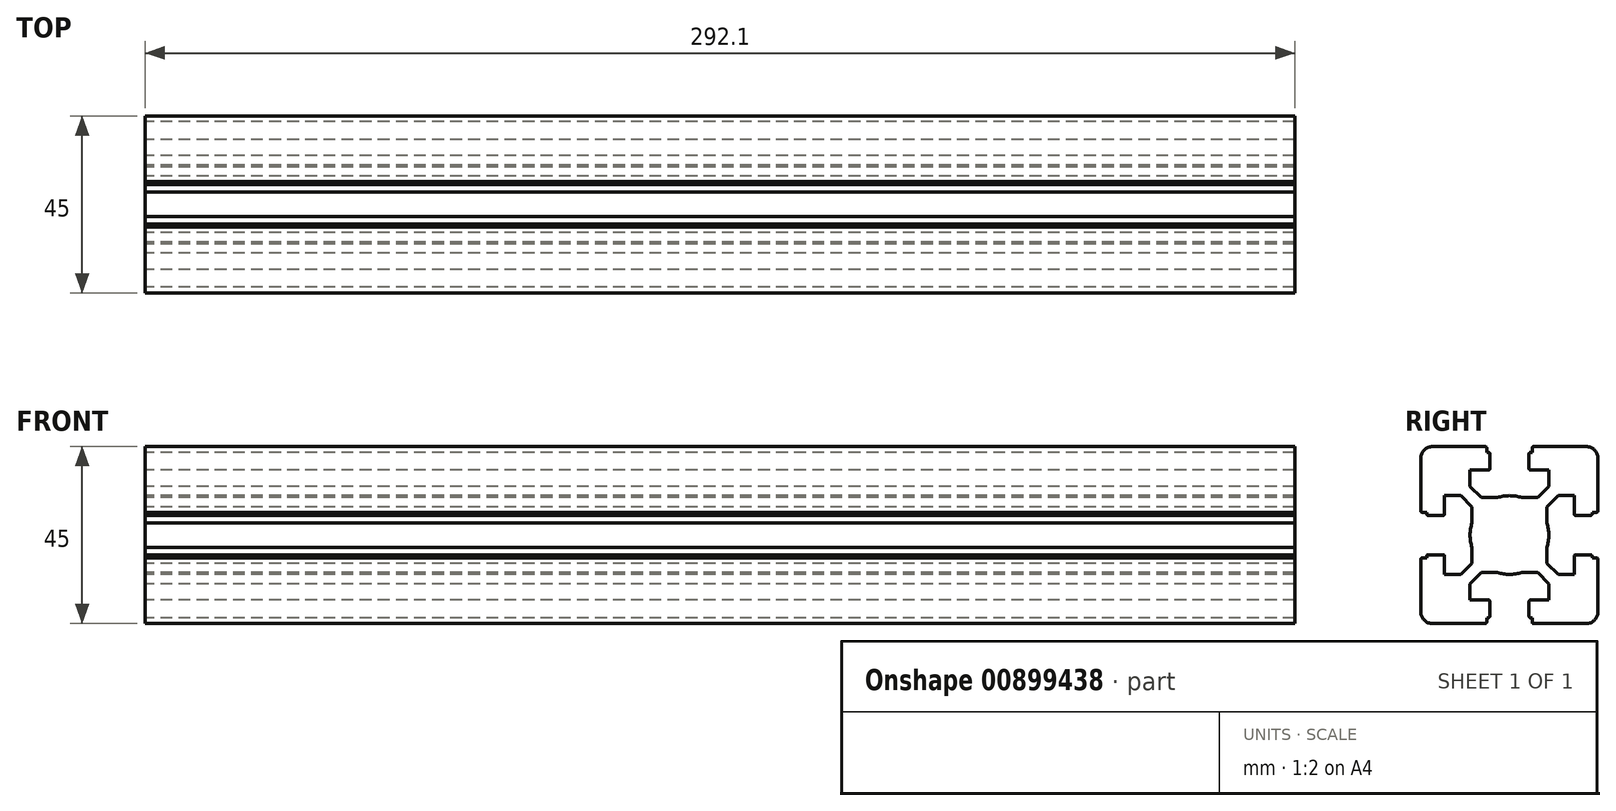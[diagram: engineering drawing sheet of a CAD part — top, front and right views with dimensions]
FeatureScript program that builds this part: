
annotation { "Feature Type Name" : "Feature", "Feature Type Description" : "" }
export const myFeature = defineFeature(function(context is Context, id is Id, definition is map)
    precondition{}
    {
        {
            var Q0;
            Q0=qCreatedBy(makeId("Right.planeOp"),FACE);
            var sketch = newSketch(context, id + "F0", { "sketchPlane" : qUnion([Q0])});
            skLineSegment(sketch, "E0", {"start": v(-20.09, -10.29) * mm, "end": v(-21.29, -10.29) * mm});
            skArc(sketch, "E1", {"start": v(-21.29, -10.29) * mm, "mid": v(-21.5, -10.38) * mm, "end": v(-21.59, -10.59) * mm});
            skLineSegment(sketch, "E2", {"start": v(-21.59, -10.59) * mm, "end": v(-21.59, -23.99) * mm});
            skArc(sketch, "E3", {"start": v(-21.59, -23.99) * mm, "mid": v(-20.7, -26.11) * mm, "end": v(-18.59, -26.99) * mm});
            skLineSegment(sketch, "E4", {"start": v(-18.59, -26.99) * mm, "end": v(-5.19, -26.99) * mm});
            skArc(sketch, "E5", {"start": v(-5.19, -26.99) * mm, "mid": v(-4.98, -26.9) * mm, "end": v(-4.89, -26.69) * mm});
            skLineSegment(sketch, "E6", {"start": v(-4.89, -26.69) * mm, "end": v(-4.89, -25.49) * mm});
            skLineSegment(sketch, "E7", {"start": v(-4.89, -25.49) * mm, "end": v(-4.39, -25.49) * mm});
            skArc(sketch, "E8", {"start": v(-4.39, -25.49) * mm, "mid": v(-4.18, -25.4) * mm, "end": v(-4.09, -25.19) * mm});
            skLineSegment(sketch, "E9", {"start": v(-4.09, -25.19) * mm, "end": v(-4.09, -21.29) * mm});
            skArc(sketch, "E10", {"start": v(-4.09, -21.29) * mm, "mid": v(-4.18, -21.08) * mm, "end": v(-4.39, -20.99) * mm});
            skLineSegment(sketch, "E11", {"start": v(-4.39, -20.99) * mm, "end": v(-9.14, -20.99) * mm});
            skLineSegment(sketch, "E12", {"start": v(-9.14, -20.99) * mm, "end": v(-9.14, -16.88) * mm});
            skLineSegment(sketch, "E13", {"start": v(-9.14, -16.88) * mm, "end": v(-6.25, -13.99) * mm});
            skLineSegment(sketch, "E14", {"start": v(-6.25, -13.99) * mm, "end": v(-2.21, -13.99) * mm});
            skArc(sketch, "E15", {"start": v(-2.21, -13.99) * mm, "mid": v(0.91, -14.49) * mm, "end": v(4.03, -13.99) * mm});
            skLineSegment(sketch, "E16", {"start": v(-20.09, -10.29) * mm, "end": v(-20.09, -9.79) * mm});
            skArc(sketch, "E17", {"start": v(-20.09, -9.79) * mm, "mid": v(-20, -9.58) * mm, "end": v(-19.79, -9.49) * mm});
            skLineSegment(sketch, "E18", {"start": v(-19.79, -9.49) * mm, "end": v(-15.89, -9.49) * mm});
            skArc(sketch, "E19", {"start": v(-15.89, -9.49) * mm, "mid": v(-15.68, -9.58) * mm, "end": v(-15.59, -9.79) * mm});
            skLineSegment(sketch, "E20", {"start": v(-15.59, -9.79) * mm, "end": v(-15.59, -14.54) * mm});
            skLineSegment(sketch, "E21", {"start": v(-15.59, -14.54) * mm, "end": v(-11.48, -14.54) * mm});
            skLineSegment(sketch, "E22", {"start": v(-11.48, -14.54) * mm, "end": v(-8.59, -11.65) * mm});
            skLineSegment(sketch, "E23", {"start": v(-8.59, -11.65) * mm, "end": v(-8.59, -7.61) * mm});
            skLineSegment(sketch, "E24", {"start": v(29.82, -4.49) * mm, "end": v(-31.05, -4.49) * mm});
            skLineSegment(sketch, "E25.MirrorCS", {"start": v(6.71, -25.49) * mm, "end": v(6.21, -25.49) * mm});
            skArc(sketch, "E26.MirrorCS", {"start": v(7.01, -26.99) * mm, "mid": v(6.8, -26.9) * mm, "end": v(6.71, -26.69) * mm});
            skLineSegment(sketch, "E27.MirrorCS", {"start": v(10.41, -11.65) * mm, "end": v(10.41, -7.61) * mm});
            skArc(sketch, "E28.MirrorCS", {"start": v(6.21, -25.49) * mm, "mid": v(6, -25.4) * mm, "end": v(5.91, -25.19) * mm});
            skLineSegment(sketch, "E29.MirrorCS", {"start": v(6.71, -26.69) * mm, "end": v(6.71, -25.49) * mm});
            skArc(sketch, "E30.MirrorCS", {"start": v(5.91, -21.29) * mm, "mid": v(6, -21.08) * mm, "end": v(6.21, -20.99) * mm});
            skLineSegment(sketch, "E31.MirrorCS", {"start": v(10.96, -16.88) * mm, "end": v(8.07, -13.99) * mm});
            skLineSegment(sketch, "E32.MirrorCS", {"start": v(13.3, -14.54) * mm, "end": v(10.41, -11.65) * mm});
            skLineSegment(sketch, "E33.MirrorCS", {"start": v(17.41, -14.54) * mm, "end": v(13.3, -14.54) * mm});
            skLineSegment(sketch, "E34.MirrorCS", {"start": v(17.41, -9.79) * mm, "end": v(17.41, -14.54) * mm});
            skLineSegment(sketch, "E35.MirrorCS", {"start": v(6.21, -20.99) * mm, "end": v(10.96, -20.99) * mm});
            skLineSegment(sketch, "E36.MirrorCS", {"start": v(8.07, -13.99) * mm, "end": v(4.03, -13.99) * mm});
            skArc(sketch, "E37.MirrorCS", {"start": v(4.03, -13.99) * mm, "mid": v(0.91, -14.49) * mm, "end": v(-2.21, -13.99) * mm});
            skLineSegment(sketch, "E38.MirrorCS", {"start": v(10.96, -20.99) * mm, "end": v(10.96, -16.88) * mm});
            skLineSegment(sketch, "E39.MirrorCS", {"start": v(5.91, -25.19) * mm, "end": v(5.91, -21.29) * mm});
            skArc(sketch, "E40.MirrorCS", {"start": v(23.41, -23.99) * mm, "mid": v(22.53, -26.11) * mm, "end": v(20.41, -26.99) * mm});
            skLineSegment(sketch, "E41.MirrorCS", {"start": v(20.41, -26.99) * mm, "end": v(7.01, -26.99) * mm});
            skLineSegment(sketch, "E42.MirrorCS", {"start": v(23.41, -10.59) * mm, "end": v(23.41, -23.99) * mm});
            skArc(sketch, "E43.MirrorCS", {"start": v(17.71, -9.49) * mm, "mid": v(17.5, -9.58) * mm, "end": v(17.41, -9.79) * mm});
            skArc(sketch, "E44.MirrorCS", {"start": v(23.11, -10.29) * mm, "mid": v(23.32, -10.38) * mm, "end": v(23.41, -10.59) * mm});
            skLineSegment(sketch, "E45.MirrorCS", {"start": v(21.91, -10.29) * mm, "end": v(21.91, -9.79) * mm});
            skLineSegment(sketch, "E46.MirrorCS", {"start": v(21.91, -10.29) * mm, "end": v(23.11, -10.29) * mm});
            skArc(sketch, "E47.MirrorCS", {"start": v(21.91, -9.79) * mm, "mid": v(21.82, -9.58) * mm, "end": v(21.61, -9.49) * mm});
            skLineSegment(sketch, "E48.MirrorCS", {"start": v(21.61, -9.49) * mm, "end": v(17.71, -9.49) * mm});
            skLineSegment(sketch, "E49.MirrorCS", {"start": v(6.71, 16.51) * mm, "end": v(6.21, 16.51) * mm});
            skArc(sketch, "E50.MirrorCS", {"start": v(-4.39, 16.51) * mm, "mid": v(-4.18, 16.42) * mm, "end": v(-4.09, 16.21) * mm});
            skLineSegment(sketch, "E51.MirrorCS", {"start": v(-4.89, 16.51) * mm, "end": v(-4.39, 16.51) * mm});
            skArc(sketch, "E52.MirrorCS", {"start": v(5.91, 12.31) * mm, "mid": v(6, 12.1) * mm, "end": v(6.21, 12.01) * mm});
            skLineSegment(sketch, "E53.MirrorCS", {"start": v(6.71, 17.71) * mm, "end": v(6.71, 16.51) * mm});
            skLineSegment(sketch, "E54.MirrorCS", {"start": v(-4.89, 17.71) * mm, "end": v(-4.89, 16.51) * mm});
            skArc(sketch, "E55.MirrorCS", {"start": v(-5.19, 18.01) * mm, "mid": v(-4.98, 17.92) * mm, "end": v(-4.89, 17.71) * mm});
            skArc(sketch, "E56.MirrorCS", {"start": v(-4.09, 12.31) * mm, "mid": v(-4.18, 12.1) * mm, "end": v(-4.39, 12.01) * mm});
            skArc(sketch, "E57.MirrorCS", {"start": v(7.01, 18.01) * mm, "mid": v(6.8, 17.92) * mm, "end": v(6.71, 17.71) * mm});
            skArc(sketch, "E58.MirrorCS", {"start": v(6.21, 16.51) * mm, "mid": v(6, 16.42) * mm, "end": v(5.91, 16.21) * mm});
            skArc(sketch, "E59.MirrorCS", {"start": v(23.11, 1.31) * mm, "mid": v(23.32, 1.4) * mm, "end": v(23.41, 1.61) * mm});
            skLineSegment(sketch, "E60.MirrorCS", {"start": v(21.91, 1.31) * mm, "end": v(21.91, 0.81) * mm});
            skArc(sketch, "E61.MirrorCS", {"start": v(-15.89, 0.51) * mm, "mid": v(-15.68, 0.6) * mm, "end": v(-15.59, 0.81) * mm});
            skArc(sketch, "E62.MirrorCS", {"start": v(-21.29, 1.31) * mm, "mid": v(-21.5, 1.4) * mm, "end": v(-21.59, 1.61) * mm});
            skArc(sketch, "E63.MirrorCS", {"start": v(17.71, 0.51) * mm, "mid": v(17.5, 0.6) * mm, "end": v(17.41, 0.81) * mm});
            skArc(sketch, "E64.MirrorCS", {"start": v(21.91, 0.81) * mm, "mid": v(21.82, 0.6) * mm, "end": v(21.61, 0.51) * mm});
            skLineSegment(sketch, "E65.MirrorCS", {"start": v(21.91, 1.31) * mm, "end": v(23.11, 1.31) * mm});
            skArc(sketch, "E66.MirrorCS", {"start": v(14.31, 5.31) * mm, "mid": v(14.1, 5.4) * mm, "end": v(14.01, 5.61) * mm});
            skArc(sketch, "E67.MirrorCS", {"start": v(-20.09, 0.81) * mm, "mid": v(-20, 0.6) * mm, "end": v(-19.79, 0.51) * mm});
            skLineSegment(sketch, "E68.MirrorCS", {"start": v(-20.09, 1.31) * mm, "end": v(-21.29, 1.31) * mm});
            skLineSegment(sketch, "E69.MirrorCS", {"start": v(-20.09, 1.31) * mm, "end": v(-20.09, 0.81) * mm});
            skLineSegment(sketch, "E70.MirrorCS", {"start": v(8.07, 5.01) * mm, "end": v(4.03, 5.01) * mm});
            skLineSegment(sketch, "E71.MirrorCS", {"start": v(-4.09, 16.21) * mm, "end": v(-4.09, 12.31) * mm});
            skLineSegment(sketch, "E72.MirrorCS", {"start": v(-9.14, 12.01) * mm, "end": v(-9.14, 7.9) * mm});
            skLineSegment(sketch, "E73.MirrorCS", {"start": v(-15.59, 5.56) * mm, "end": v(-11.48, 5.56) * mm});
            skLineSegment(sketch, "E74.MirrorCS", {"start": v(-4.39, 12.01) * mm, "end": v(-9.14, 12.01) * mm});
            skLineSegment(sketch, "E75.MirrorCS", {"start": v(-9.14, 7.9) * mm, "end": v(-6.25, 5.01) * mm});
            skLineSegment(sketch, "E76.MirrorCS", {"start": v(10.96, 12.01) * mm, "end": v(10.96, 7.9) * mm});
            skArc(sketch, "E77.MirrorCS", {"start": v(-21.59, 15.01) * mm, "mid": v(-20.7, 17.13) * mm, "end": v(-18.59, 18.01) * mm});
            skLineSegment(sketch, "E78.MirrorCS", {"start": v(23.41, 1.61) * mm, "end": v(23.41, 15.01) * mm});
            skLineSegment(sketch, "E79.MirrorCS", {"start": v(13.3, 5.56) * mm, "end": v(10.41, 2.67) * mm});
            skLineSegment(sketch, "E80.MirrorCS", {"start": v(-8.59, 2.67) * mm, "end": v(-8.59, -1.37) * mm});
            skLineSegment(sketch, "E81.MirrorCS", {"start": v(-15.59, 0.81) * mm, "end": v(-15.59, 5.56) * mm});
            skLineSegment(sketch, "E82.MirrorCS", {"start": v(10.41, 2.67) * mm, "end": v(10.41, -1.37) * mm});
            skLineSegment(sketch, "E83.MirrorCS", {"start": v(-18.59, 18.01) * mm, "end": v(-5.19, 18.01) * mm});
            skLineSegment(sketch, "E84.MirrorCS", {"start": v(10.96, 7.9) * mm, "end": v(8.07, 5.01) * mm});
            skLineSegment(sketch, "E85.MirrorCS", {"start": v(17.41, 5.56) * mm, "end": v(13.3, 5.56) * mm});
            skArc(sketch, "E86.MirrorCS", {"start": v(23.41, 15.01) * mm, "mid": v(22.53, 17.13) * mm, "end": v(20.41, 18.01) * mm});
            skLineSegment(sketch, "E87.MirrorCS", {"start": v(5.91, 16.21) * mm, "end": v(5.91, 12.31) * mm});
            skLineSegment(sketch, "E88.MirrorCS", {"start": v(17.41, 0.81) * mm, "end": v(17.41, 5.56) * mm});
            skLineSegment(sketch, "E89.MirrorCS", {"start": v(-11.48, 5.56) * mm, "end": v(-8.59, 2.67) * mm});
            skLineSegment(sketch, "E90.MirrorCS", {"start": v(-6.25, 5.01) * mm, "end": v(-2.21, 5.01) * mm});
            skLineSegment(sketch, "E91.MirrorCS", {"start": v(-21.59, 1.61) * mm, "end": v(-21.59, 15.01) * mm});
            skArc(sketch, "E92.MirrorCS", {"start": v(4.03, 5.01) * mm, "mid": v(0.91, 5.51) * mm, "end": v(-2.21, 5.01) * mm});
            skLineSegment(sketch, "E93.MirrorCS", {"start": v(6.21, 12.01) * mm, "end": v(10.96, 12.01) * mm});
            skArc(sketch, "E94.MirrorCS", {"start": v(-2.21, 5.01) * mm, "mid": v(0.91, 5.51) * mm, "end": v(4.03, 5.01) * mm});
            skLineSegment(sketch, "E95.MirrorCS", {"start": v(20.41, 18.01) * mm, "end": v(7.01, 18.01) * mm});
            skLineSegment(sketch, "E96.MirrorCS", {"start": v(-19.79, 0.51) * mm, "end": v(-15.89, 0.51) * mm});
            skLineSegment(sketch, "E97.MirrorCS", {"start": v(21.61, 0.51) * mm, "end": v(17.71, 0.51) * mm});
            skLineSegment(sketch, "E98.MirrorCS", {"start": v(0.91, -27.65) * mm, "end": v(0.91, 19.82) * mm});
            skArc(sketch, "E99", {"start": v(-8.59, -1.37) * mm, "mid": v(-9.09, -4.49) * mm, "end": v(-8.59, -7.61) * mm});
            skArc(sketch, "E100", {"start": v(10.41, -7.61) * mm, "mid": v(10.91, -4.49) * mm, "end": v(10.41, -1.37) * mm});
            skSolve(sketch);
        }
        {
            var Q0;
            Q0=qSketchRegion(id+"F0",true);
            extrude(context, id + "F1", {"entities" : qUnion([Q0]), "depth" : 292.1 * mm, "offsetDistance" : 25.4 * mm});
        }
    });
